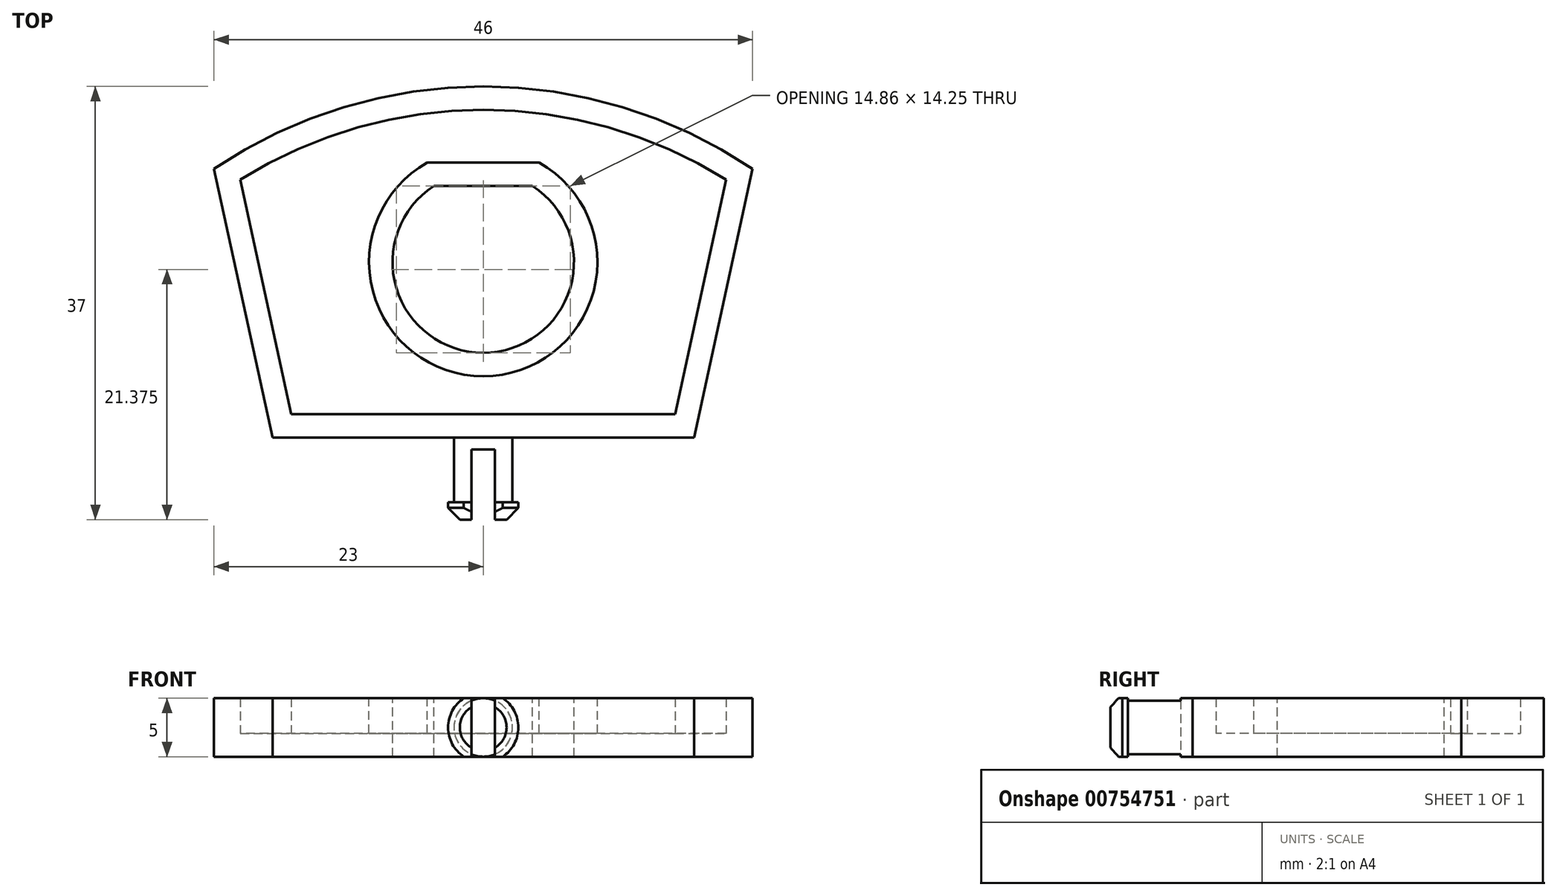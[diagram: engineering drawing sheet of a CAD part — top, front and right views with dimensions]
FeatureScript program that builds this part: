
annotation { "Feature Type Name" : "Feature", "Feature Type Description" : "" }
export const myFeature = defineFeature(function(context is Context, id is Id, definition is map)
    precondition{}
    {
        {
            var Q0;
            Q0=qCreatedBy(makeId("Top.planeOp"),FACE);
            var sketch = newSketch(context, id + "F0", { "sketchPlane" : qUnion([Q0])});
            skLineSegment(sketch, "E0", {"start": v(-23, 22.97) * mm, "end": v(-18, 0) * mm});
            skLineSegment(sketch, "E1", {"start": v(-18, 0) * mm, "end": v(18, 0) * mm});
            skLineSegment(sketch, "E2", {"start": v(18, 0) * mm, "end": v(23, 22.97) * mm});
            skArc(sketch, "E3", {"start": v(23, 22.97) * mm, "mid": v(0, 30) * mm, "end": v(-23, 22.97) * mm});
            skSolve(sketch);
        }
        {
            var Q0;
            Q0 = qSketchRegion(id + "F0", true);
            extrude(context, id + "F1", {"entities" : qUnion([Q0]), "depth" : 5 * mm, "offsetDistance" : 25 * mm, "symmetric" : true});
        }
        {
            var Q0;
            Q0=makeQuery(id+"F1.opExtrude","CAP_FACE",FACE,{"disambiguationData":[OSD([sQuery(id+"F0.wireOp",EDGE,"E0"),sQuery(id+"F0.wireOp",EDGE,"E1"),sQuery(id+"F0.wireOp",EDGE,"E2"),sQuery(id+"F0.wireOp",EDGE,"E3")])],"isStart":false});
            var sketch = newSketch(context, id + "F2", { "sketchPlane" : qUnion([Q0])});
            skLineSegment(sketch, "E4", {"start": v(-4.22, 21.5) * mm, "end": v(4.22, 21.5) * mm});
            skArc(sketch, "E5", {"start": v(-4.22, 21.5) * mm, "mid": v(0, 7.25) * mm, "end": v(4.22, 21.5) * mm});
            skSolve(sketch);
        }
        {
            var Q0;
            Q0 = qSketchRegion(id + "F2", true);
            extrude(context, id + "F3", {"entities" : qUnion([Q0]), "operationType" : NewBodyOperationType.REMOVE, "endBound" : BoundingType.UP_TO_NEXT, "oppositeDirection" : true, "depth" : 25 * mm, "offsetDistance" : 25 * mm});
        }
        {
            var Q0;
            Q0=makeQuery(id+"F1.opExtrude","CAP_FACE",FACE,{"disambiguationData":[OSD([sQuery(id+"F0.wireOp",EDGE,"E0"),sQuery(id+"F0.wireOp",EDGE,"E1"),sQuery(id+"F0.wireOp",EDGE,"E2"),sQuery(id+"F0.wireOp",EDGE,"E3")])],"isStart":false});
            shell(context, id + "F4", {"entities" : qUnion([Q0]), "thickness" : 2 * mm});
        }
        {
            var Q0;
            Q0=qCreatedBy(makeId("Right.planeOp"),FACE);
            var sketch = newSketch(context, id + "F5", { "sketchPlane" : qUnion([Q0])});
            skLineSegment(sketch, "E6", {"start": v(0, 0) * mm, "end": v(-7, 0) * mm});
            skLineSegment(sketch, "E7", {"start": v(-7, 0) * mm, "end": v(-7, 3) * mm});
            skLineSegment(sketch, "E8", {"start": v(-7, 3) * mm, "end": v(-5.5, 3) * mm});
            skLineSegment(sketch, "E9", {"start": v(-5.5, 3) * mm, "end": v(-5.5, 2.5) * mm});
            skLineSegment(sketch, "E10", {"start": v(-5.5, 2.5) * mm, "end": v(0, 2.5) * mm});
            skLineSegment(sketch, "E11", {"start": v(0, 2.5) * mm, "end": v(0, 0) * mm});
            skSolve(sketch);
        }
        {
            var Q0;
            Q0=makeQuery(id+"F5.imprint","IMPRINT",FACE,{"disambiguationData":[TD([[makeQuery(id+"F5.imprint","IMPRINT",EDGE,{"derivedFrom":sQuery(id+"F5.wireOp",EDGE,"E6")}),-1.0]])]});
            var Q1;
            Q1=sQuery(id+"F5.wireOp",EDGE,"E6");
            revolve(context, id + "F6", {"operationType" : NewBodyOperationType.ADD, "surfaceOperationType" : NewSurfaceOperationType.NEW, "entities" : qUnion([Q0]), "axis" : qUnion([Q1]), "revolveType" : RevolveType.FULL});
        }
        {
            var Q0;
            Q0=makeQuery(id+"F6.opRevolve","SWEPT_EDGE",EDGE,{"disambiguationData":[OSD([sQuery(id+"F5.wireOp",EDGE,"E7"),sQuery(id+"F5.wireOp",EDGE,"E8")])]});
            chamfer(context, id + "F7", {"entities" : qUnion([Q0]), "width" : 1 * mm, "tangentPropagation" : true});
        }
        {
            var Q0;
            Q0=makeQuery(id+"F6.opRevolve","SWEPT_FACE",FACE,{"disambiguationData":[OSD([sQuery(id+"F5.wireOp",EDGE,"E7")])]});
            var sketch = newSketch(context, id + "F8", { "sketchPlane" : qUnion([Q0])});
            skLineSegment(sketch, "E12.bottom", {"start": v(-25.05, 2.5) * mm, "end": v(24.08, 2.5) * mm});
            skLineSegment(sketch, "E12.top", {"start": v(-25.05, -2.5) * mm, "end": v(24.08, -2.5) * mm});
            skLineSegment(sketch, "E12.left", {"start": v(-25.05, 2.5) * mm, "end": v(-25.05, -2.5) * mm});
            skLineSegment(sketch, "E12.right", {"start": v(24.08, 2.5) * mm, "end": v(24.08, -2.5) * mm});
            skSolve(sketch);
        }
        {
            var Q0;
            Q0 = qSketchRegion(id + "F8", true);
            extrude(context, id + "F9", {"entities" : qUnion([Q0]), "operationType" : NewBodyOperationType.INTERSECT, "endBound" : BoundingType.THROUGH_ALL, "oppositeDirection" : true, "depth" : 25 * mm, "offsetDistance" : 25 * mm});
        }
        {
            var Q0;
            Q0=makeQuery(id+"F6.opRevolve","SWEPT_FACE",FACE,{"disambiguationData":[OSD([sQuery(id+"F5.wireOp",EDGE,"E7")])]});
            var sketch = newSketch(context, id + "F10", { "sketchPlane" : qUnion([Q0])});
            skLineSegment(sketch, "E13.bottom", {"start": v(-1, 4.38) * mm, "end": v(1, 4.38) * mm});
            skLineSegment(sketch, "E13.top", {"start": v(-1, -4.23) * mm, "end": v(1, -4.23) * mm});
            skLineSegment(sketch, "E13.left", {"start": v(-1, 4.38) * mm, "end": v(-1, -4.23) * mm});
            skLineSegment(sketch, "E13.right", {"start": v(1, 4.38) * mm, "end": v(1, -4.23) * mm});
            skSolve(sketch);
        }
        {
            var Q0;
            Q0 = qSketchRegion(id + "F10", true);
            extrude(context, id + "F11", {"entities" : qUnion([Q0]), "operationType" : NewBodyOperationType.REMOVE, "oppositeDirection" : true, "depth" : 6 * mm, "offsetDistance" : 25 * mm});
        }
    });
